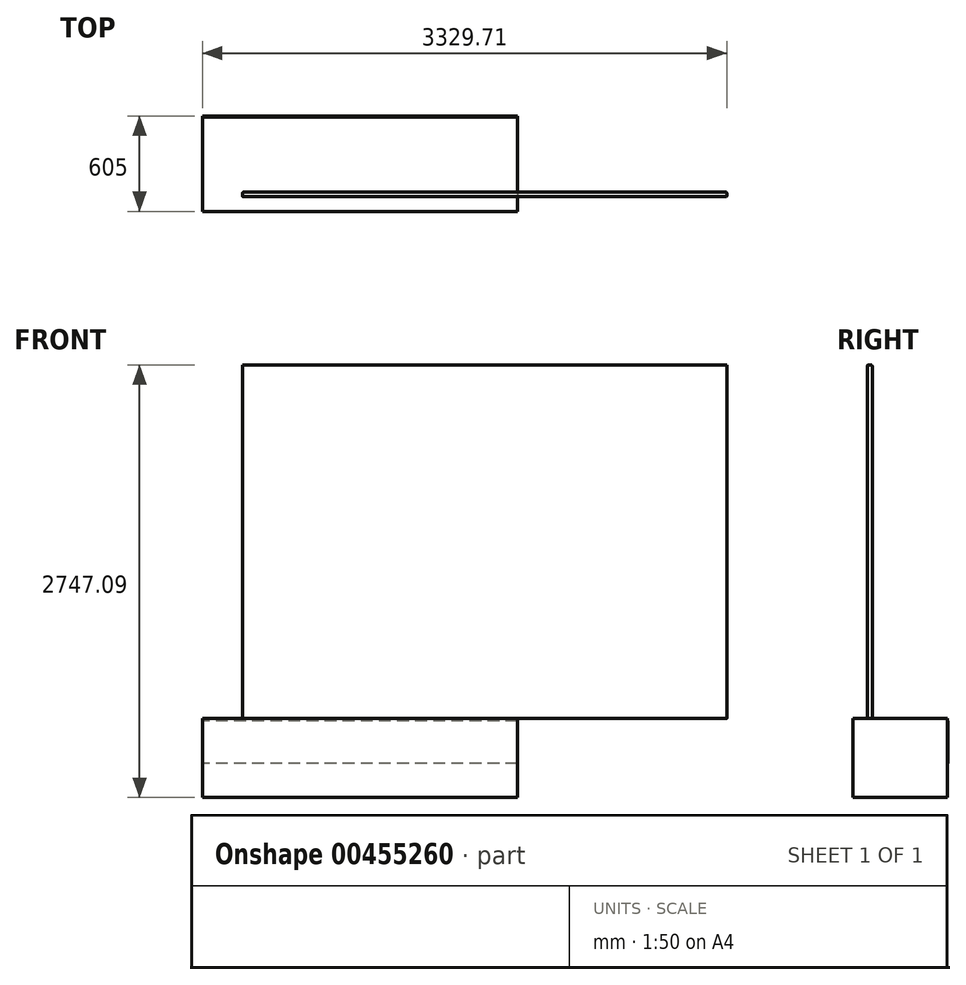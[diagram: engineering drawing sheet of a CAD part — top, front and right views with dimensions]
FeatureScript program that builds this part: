
annotation { "Feature Type Name" : "Feature", "Feature Type Description" : "" }
export const myFeature = defineFeature(function(context is Context, id is Id, definition is map)
    precondition{}
    {
        {
            var Q0;
            Q0=qCreatedBy(makeId("Top.planeOp"),FACE);
            var sketch = newSketch(context, id + "F0", { "sketchPlane" : qUnion([Q0])});
            skLineSegment(sketch, "E0.bottom", {"start": v(-96.87, 555.82) * mm, "end": v(1903.13, 555.82) * mm});
            skLineSegment(sketch, "E0.top", {"start": v(-96.87, -44.18) * mm, "end": v(1903.13, -44.18) * mm});
            skLineSegment(sketch, "E0.left", {"start": v(-96.87, 555.82) * mm, "end": v(-96.87, -44.18) * mm});
            skLineSegment(sketch, "E0.right", {"start": v(1903.13, 555.82) * mm, "end": v(1903.13, -44.18) * mm});
            skSolve(sketch);
        }
        {
            var Q0;
            Q0=makeQuery(id+"F0.imprint","IMPRINT",FACE,{"disambiguationData":[TD([[makeQuery(id+"F0.imprint","IMPRINT",EDGE,{"derivedFrom":sQuery(id+"F0.wireOp",EDGE,"E0.bottom")}),-1.0]])]});
            extrude(context, id + "F1", {"entities" : qUnion([Q0]), "depth" : 500 * mm});
        }
        {
            var Q0;
            Q0=makeQuery(id+"F1.opExtrude","CAP_FACE",FACE,{"disambiguationData":[OSD([sQuery(id+"F0.wireOp",EDGE,"E0.bottom"),sQuery(id+"F0.wireOp",EDGE,"E0.top"),sQuery(id+"F0.wireOp",EDGE,"E0.left"),sQuery(id+"F0.wireOp",EDGE,"E0.right")])],"isStart":false});
            var sketch = newSketch(context, id + "F2", { "sketchPlane" : qUnion([Q0])});
            skLineSegment(sketch, "E1.bottom", {"start": v(156.04, 79.49) * mm, "end": v(3232.84, 79.49) * mm});
            skLineSegment(sketch, "E1.top", {"start": v(156.04, 49.49) * mm, "end": v(3232.84, 49.49) * mm});
            skLineSegment(sketch, "E1.left", {"start": v(156.04, 79.49) * mm, "end": v(156.04, 49.49) * mm});
            skLineSegment(sketch, "E1.right", {"start": v(3232.84, 79.49) * mm, "end": v(3232.84, 49.49) * mm});
            skSolve(sketch);
        }
        {
            var Q0;
            Q0=makeQuery(id+"F2.imprint","IMPRINT",FACE,{"disambiguationData":[TD([[makeQuery(id+"F2.imprint","IMPRINT",EDGE,{"derivedFrom":sQuery(id+"F2.wireOp",EDGE,"E1.bottom")}),-1.0]])]});
            extrude(context, id + "F3", {"entities" : qUnion([Q0]), "flatOperationType" : FlatOperationType.REMOVE, "offsetDistance" : 25 * mm, "depth" : 2247.1 * mm, "domain" : OperationDomain.MODEL});
        }
        {
            var Q0;
            Q0=makeQuery(id+"F3.opExtrude","SWEPT_FACE",FACE,{"disambiguationData":[OSD([sQuery(id+"F2.wireOp",EDGE,"E1.bottom")])]});
            fillet(context, id + "F4", {"entities" : qUnion([Q0]), "radius" : 10 * mm, "tangentPropagation" : true, "allowEdgeOverflow" : false});
        }
        {
            var Q0;
            Q0=makeQuery(id+"F3.opExtrude","SWEPT_FACE",FACE,{"disambiguationData":[OSD([sQuery(id+"F2.wireOp",EDGE,"E1.top")])]});
            fillet(context, id + "F5", {"entities" : qUnion([Q0]), "radius" : 5 * mm, "tangentPropagation" : true, "allowEdgeOverflow" : false});
        }
        {
            var Q0;
            Q0=makeQuery(id+"F1.opExtrude","SWEPT_FACE",FACE,{"disambiguationData":[OSD([sQuery(id+"F0.wireOp",EDGE,"E0.bottom")])]});
            var sketch = newSketch(context, id + "F6", { "sketchPlane" : qUnion([Q0])});
            skLineSegment(sketch, "E2.bottom", {"start": v(-1903.13, 485.88) * mm, "end": v(96.87, 485.88) * mm});
            skLineSegment(sketch, "E2.top", {"start": v(-1903.13, 216.2) * mm, "end": v(96.87, 216.2) * mm});
            skLineSegment(sketch, "E2.left", {"start": v(-1903.13, 485.88) * mm, "end": v(-1903.13, 216.2) * mm});
            skLineSegment(sketch, "E2.right", {"start": v(96.87, 485.88) * mm, "end": v(96.87, 216.2) * mm});
            skSolve(sketch);
        }
        {
            var Q0;
            Q0=makeQuery(id+"F6.imprint","IMPRINT",FACE,{"disambiguationData":[TD([[makeQuery(id+"F6.imprint","IMPRINT",EDGE,{"derivedFrom":sQuery(id+"F6.wireOp",EDGE,"E2.bottom")}),-1.0]])]});
            extrude(context, id + "F7", {"entities" : qUnion([Q0]), "depth" : 5 * mm});
        }
    });
